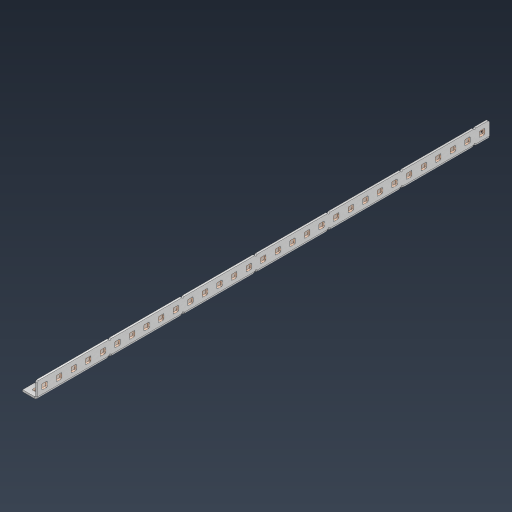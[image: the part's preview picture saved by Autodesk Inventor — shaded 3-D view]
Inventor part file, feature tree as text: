
AUTODESK INVENTOR PART (.ipt)
format: ipt  version: 2024.3 (Build 283343000, 343)  size: 1,162,240 bytes
history: native  units: in
note: dims shown in document units (in); Inventor stores cm internally (conversion verified against a paired STEP export)
features: other x100, extrude x91, sheet_metal_op x11, pattern_linear x2, mirror x1, chamfer x1, sketch x1
ambient origin geometry x8: Origin, YZ Plane, XZ Plane, XY Plane, X Axis, Y Axis, Z Axis, Center Point
bodies: Solid1 (feature_tree), Body (feature_tree)
feature tree (207):
  sheet_metal_op  "Flanges"
  other  "Flange Pattern Plane"
  other  "Flange Pattern Sketch"
  sheet_metal_op  "Flange Pattern"
  sheet_metal_op  "Body Pattern"
  pattern_linear  "Center Pattern"  Spacing1=15.5in  [1 undecoded]
  other  "Arc Length"
  mirror  "Notch Mirror"
  pattern_linear  "Notch Pattern"  Spacing1=0.0625in  [1 undecoded]
  chamfer  "End Chamfer"
  extrude  "Half Cut"  Depth=0.0625in
  other  "Plate1"
  sketch  "Sketch2"  dims[d0=1.0in d1=15.5in d2=0.0625in d3=0.0625in d4=0.0312in d5=0.125in d6=0.0625in d7=0.5in d8=90.0deg d9=0.0312in d10=0.25in d11=0.0625in d12=0.0625in d16=0.182in d17=0.02in d18=0.0625in d19=0.0in d20=0.25in d21=0.25in d38=12.2047in d40=0.5in d41=0.3937in d43=1.0in d46=0.172in d47=1.0in d48=0.0in d49=0.182in d50=0.02in d51=0.25in d52=0.25in d53=0.0625in d54=0.0in d55=0.172in d56=1.0in d57=0.0in d58=0.25in d60=12.2047in d62=0.5in d63=0.3937in d65=0.5in d85=0.1473in d86=0.1782in d88=0.04in d89=0.0625in d90=0.0in d91=0.04in d92=0.0491in d95=2.5in d96=0.04in d97=0.25in d98=45.0deg d99=0.25in d100=0.5in d101=0.0in d102=2.497in d106=0.182in d107=0.02in d108=0.5in d109=0.5in d110=0.0625in d111=0.0in d112=0.172in d113=0.5in d114=0.0in d117=0.5in d118=0.5in d119=0.5in]
  other  "Plate2"
  sheet_metal_op  "Bend1"
  sheet_metal_op  "Corner1"
  other  "Srf1"
  other  "Srf2"
  other  "Srf91"
  sheet_metal_op  "Body Pattern Sketch"
  other  "Srf92"
  other  "Srf786"
  other  "Srf823"
  other  "Srf824"
  other  "Srf825"
  other  "Srf826"
  other  "Srf827"
  other  "Srf828"
  other  "Srf829"
  other  "Srf856"
  other  "Srf857"
  other  "Srf858"
  other  "Srf859"
  other  "Srf860"
  other  "Srf861"
  other  "Srf862"
  other  "Srf889"
  other  "Srf890"
  other  "Srf891"
  other  "Srf892"
  other  "Srf893"
  other  "Srf894"
  other  "Srf895"
  other  "Srf896"
  other  "Srf922"
  other  "Srf923"
  other  "Srf924"
  other  "Srf925"
  other  "Srf926"
  other  "Srf959"
  other  "Srf960"
  other  "Srf961"
  other  "Srf962"
  other  "Srf963"
  other  "Srf996"
  other  "Srf997"
  other  "Srf998"
  other  "Srf999"
  other  "Srf1000"
  other  "Srf1143"
  other  "Srf1144"
  other  "Srf1145"
  other  "Srf1146"
  other  "Srf1147"
  other  "Srf1148"
  other  "Srf1149"
  other  "Srf1150"
  other  "Srf1151"
  other  "Srf1152"
  other  "Srf1153"
  other  "Srf1154"
  other  "Srf1155"
  other  "Srf1156"
  other  "Srf1157"
  other  "Srf1158"
  other  "Srf1159"
  other  "Srf1199"
  other  "Srf1200"
  other  "Srf1201"
  other  "Srf1202"
  other  "Srf1203"
  other  "Srf1204"
  other  "Srf1205"
  other  "Srf1206"
  other  "Srf1207"
  other  "Srf1208"
  other  "Srf1209"
  other  "Srf1210"
  other  "Srf1211"
  other  "Srf1212"
  other  "Srf1213"
  other  "Srf1214"
  other  "Srf1215"
  other  "Srf1255"
  other  "Srf1256"
  other  "Srf1257"
  other  "Srf1258"
  other  "Srf1259"
  other  "Srf1260"
  other  "Srf1261"
  other  "Srf1262"
  other  "Srf1263"
  other  "Srf1264"
  other  "Srf1265"
  other  "Srf1266"
  other  "Srf1267"
  other  "Srf1268"
  other  "Srf1269"
  other  "Srf1270"
  other  "Srf1271"
  sheet_metal_op  "Flange Stamp"
  sheet_metal_op  "Flange Circle"
  sheet_metal_op  "Body Stamp"
  sheet_metal_op  "Body Circle"
  other  "Center Stamp"
  other  "Center Circle"
  sheet_metal_op  "Notch"
  extrude  "ExtrusionSrf2"  Depth=0.0312in
  extrude  "ExtrusionSrf92"  Depth=0.5in
  extrude  "ExtrusionSrf823"  Depth=0.0625in
  extrude  "ExtrusionSrf824"  Depth=0.5in TaperAngle=90.0deg
  extrude  "ExtrusionSrf825"  Depth=0.5in
  extrude  "ExtrusionSrf826"  Depth=0.0625in
  extrude  "ExtrusionSrf827"  Depth=0.0625in
  extrude  "ExtrusionSrf828"  Depth=0.182in
  extrude  "ExtrusionSrf829"  Depth=0.02in
  extrude  "ExtrusionSrf856"  Depth=0.0625in
  extrude  "ExtrusionSrf857"  TaperAngle=0.0deg  [1 undecoded]
  extrude  "ExtrusionSrf858"  Depth=0.5in
  extrude  "ExtrusionSrf859"  Depth=0.5in
  extrude  "ExtrusionSrf860"  Depth=0.5in
  extrude  "ExtrusionSrf861"  Depth=0.5in
  extrude  "ExtrusionSrf862"  Depth=1.0in TaperAngle=0.0deg
  extrude  "ExtrusionSrf889"  Depth=0.182in
  extrude  "ExtrusionSrf890"  Depth=0.02in
  extrude  "ExtrusionSrf891"  Depth=0.5in
  extrude  "ExtrusionSrf892"  Depth=0.5in
  extrude  "ExtrusionSrf893"  Depth=0.0625in
  extrude  "ExtrusionSrf894"  TaperAngle=0.0deg  [1 undecoded]
  extrude  "ExtrusionSrf895"  Depth=0.5in
  extrude  "ExtrusionSrf896"  Depth=1.0in TaperAngle=0.0deg
  extrude  "ExtrusionSrf922"  Depth=0.5in
  extrude  "ExtrusionSrf923"  Depth=0.5in
  extrude  "ExtrusionSrf924"  Depth=0.5in
  extrude  "ExtrusionSrf925"  Depth=0.5in
  extrude  "ExtrusionSrf926"  Depth=0.5in
  extrude  "ExtrusionSrf959"  Depth=0.5in
  extrude  "ExtrusionSrf960"  Depth=0.0625in
  extrude  "ExtrusionSrf961"  TaperAngle=0.0deg  [1 undecoded]
  extrude  "ExtrusionSrf962"  Depth=0.5in
  extrude  "ExtrusionSrf963"  Depth=0.5in
  extrude  "ExtrusionSrf996"  Depth=0.5in
  extrude  "ExtrusionSrf997"  Depth=0.5in TaperAngle=45.0deg
  extrude  "ExtrusionSrf998"  Depth=0.5in
  extrude  "ExtrusionSrf999"  Depth=0.5in TaperAngle=0.0deg
  extrude  "ExtrusionSrf1000"  Depth=0.5in
  extrude  "ExtrusionSrf1143"  Depth=0.182in
  extrude  "ExtrusionSrf1144"  Depth=0.02in
  extrude  "ExtrusionSrf1145"  Depth=0.5in
  extrude  "ExtrusionSrf1146"  Depth=0.5in
  extrude  "ExtrusionSrf1147"  Depth=0.0625in
  extrude  "ExtrusionSrf1148"  TaperAngle=0.0deg  [1 undecoded]
  extrude  "ExtrusionSrf1149"  Depth=0.5in
  extrude  "ExtrusionSrf1150"  Depth=0.5in TaperAngle=0.0deg
  extrude  "ExtrusionSrf1151"  Depth=0.5in
  extrude  "ExtrusionSrf1152"  Depth=0.5in
  extrude  "ExtrusionSrf1153"  Depth=0.5in
  extrude  "ExtrusionSrf1154"  [1 undecoded]
  extrude  "ExtrusionSrf1155"  [1 undecoded]
  extrude  "ExtrusionSrf1156"  [1 undecoded]
  extrude  "ExtrusionSrf1157"  [1 undecoded]
  extrude  "ExtrusionSrf1158"  [1 undecoded]
  extrude  "ExtrusionSrf1159"  [1 undecoded]
  extrude  "ExtrusionSrf1199"  [1 undecoded]
  extrude  "ExtrusionSrf1200"  [1 undecoded]
  extrude  "ExtrusionSrf1201"  [1 undecoded]
  extrude  "ExtrusionSrf1202"  [1 undecoded]
  extrude  "ExtrusionSrf1203"  [1 undecoded]
  extrude  "ExtrusionSrf1204"  [1 undecoded]
  extrude  "ExtrusionSrf1205"  [1 undecoded]
  extrude  "ExtrusionSrf1206"  [1 undecoded]
  extrude  "ExtrusionSrf1207"  [1 undecoded]
  extrude  "ExtrusionSrf1208"  [1 undecoded]
  extrude  "ExtrusionSrf1209"  [1 undecoded]
  extrude  "ExtrusionSrf1210"  [1 undecoded]
  extrude  "ExtrusionSrf1211"  [1 undecoded]
  extrude  "ExtrusionSrf1212"  [1 undecoded]
  extrude  "ExtrusionSrf1213"  [1 undecoded]
  extrude  "ExtrusionSrf1214"  [1 undecoded]
  extrude  "ExtrusionSrf1215"  [1 undecoded]
  extrude  "ExtrusionSrf1255"  [1 undecoded]
  extrude  "ExtrusionSrf1256"  [1 undecoded]
  extrude  "ExtrusionSrf1257"  [1 undecoded]
  extrude  "ExtrusionSrf1258"  [1 undecoded]
  extrude  "ExtrusionSrf1259"  [1 undecoded]
  extrude  "ExtrusionSrf1260"  [1 undecoded]
  extrude  "ExtrusionSrf1261"  [1 undecoded]
  extrude  "ExtrusionSrf1262"  [1 undecoded]
  extrude  "ExtrusionSrf1263"  [1 undecoded]
  extrude  "ExtrusionSrf1264"  [1 undecoded]
  extrude  "ExtrusionSrf1265"  [1 undecoded]
  extrude  "ExtrusionSrf1266"  [1 undecoded]
  extrude  "ExtrusionSrf1267"  [1 undecoded]
  extrude  "ExtrusionSrf1268"  [1 undecoded]
  extrude  "ExtrusionSrf1269"  [1 undecoded]
  extrude  "ExtrusionSrf1270"  [1 undecoded]
  extrude  "ExtrusionSrf1271"  [1 undecoded]
note: 46 required parameter values undecoded (feature->parameter linkage not recoverable at this tier; creation-order binding heuristic only, values carry confidence <= 0.55)
